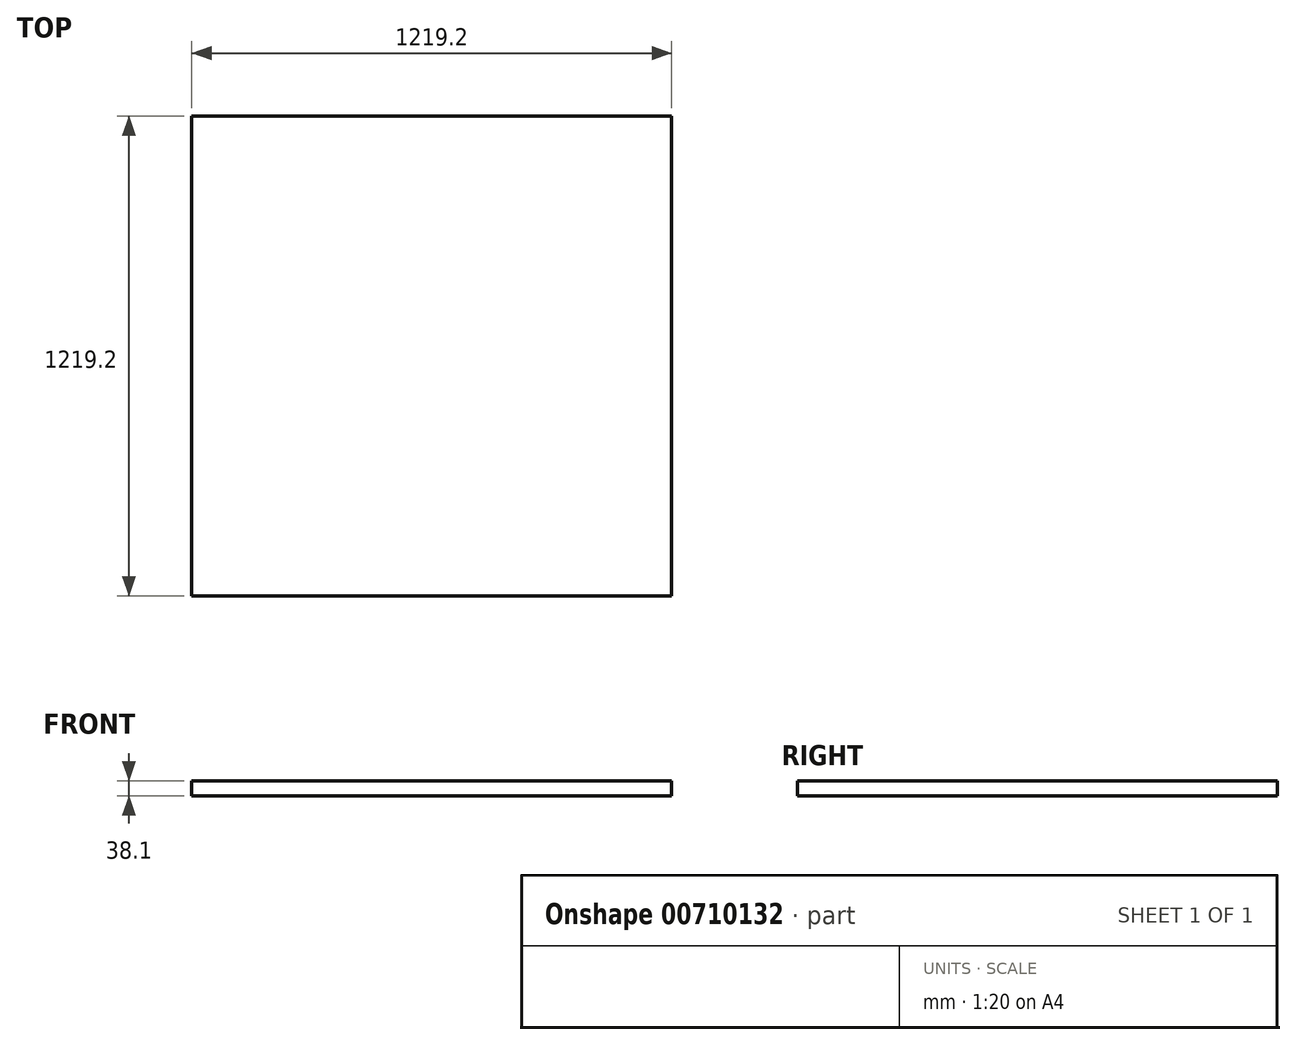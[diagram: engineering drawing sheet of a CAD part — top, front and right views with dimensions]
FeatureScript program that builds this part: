
annotation { "Feature Type Name" : "Feature", "Feature Type Description" : "" }
export const myFeature = defineFeature(function(context is Context, id is Id, definition is map)
    precondition{}
    {
        {
            var Q0;
            Q0=qCreatedBy(makeId("Right.planeOp"),FACE);
            var sketch = newSketch(context, id + "F0", { "sketchPlane" : qUnion([Q0])});
            skLineSegment(sketch, "E0.bottom", {"start": v(0, 0) * mm, "end": v(1219.2, 0) * mm});
            skLineSegment(sketch, "E0.top", {"start": v(0, 38.1) * mm, "end": v(1219.2, 38.1) * mm});
            skLineSegment(sketch, "E0.left", {"start": v(0, 0) * mm, "end": v(0, 38.1) * mm});
            skLineSegment(sketch, "E0.right", {"start": v(1219.2, 0) * mm, "end": v(1219.2, 38.1) * mm});
            skSolve(sketch);
        }
        {
            var Q0;
            Q0 = qSketchRegion(id + "F0", true);
            extrude(context, id + "F1", {"entities" : qUnion([Q0]), "depth" : 1219.2 * mm, "offsetDistance" : 25.4 * mm});
        }
    });
